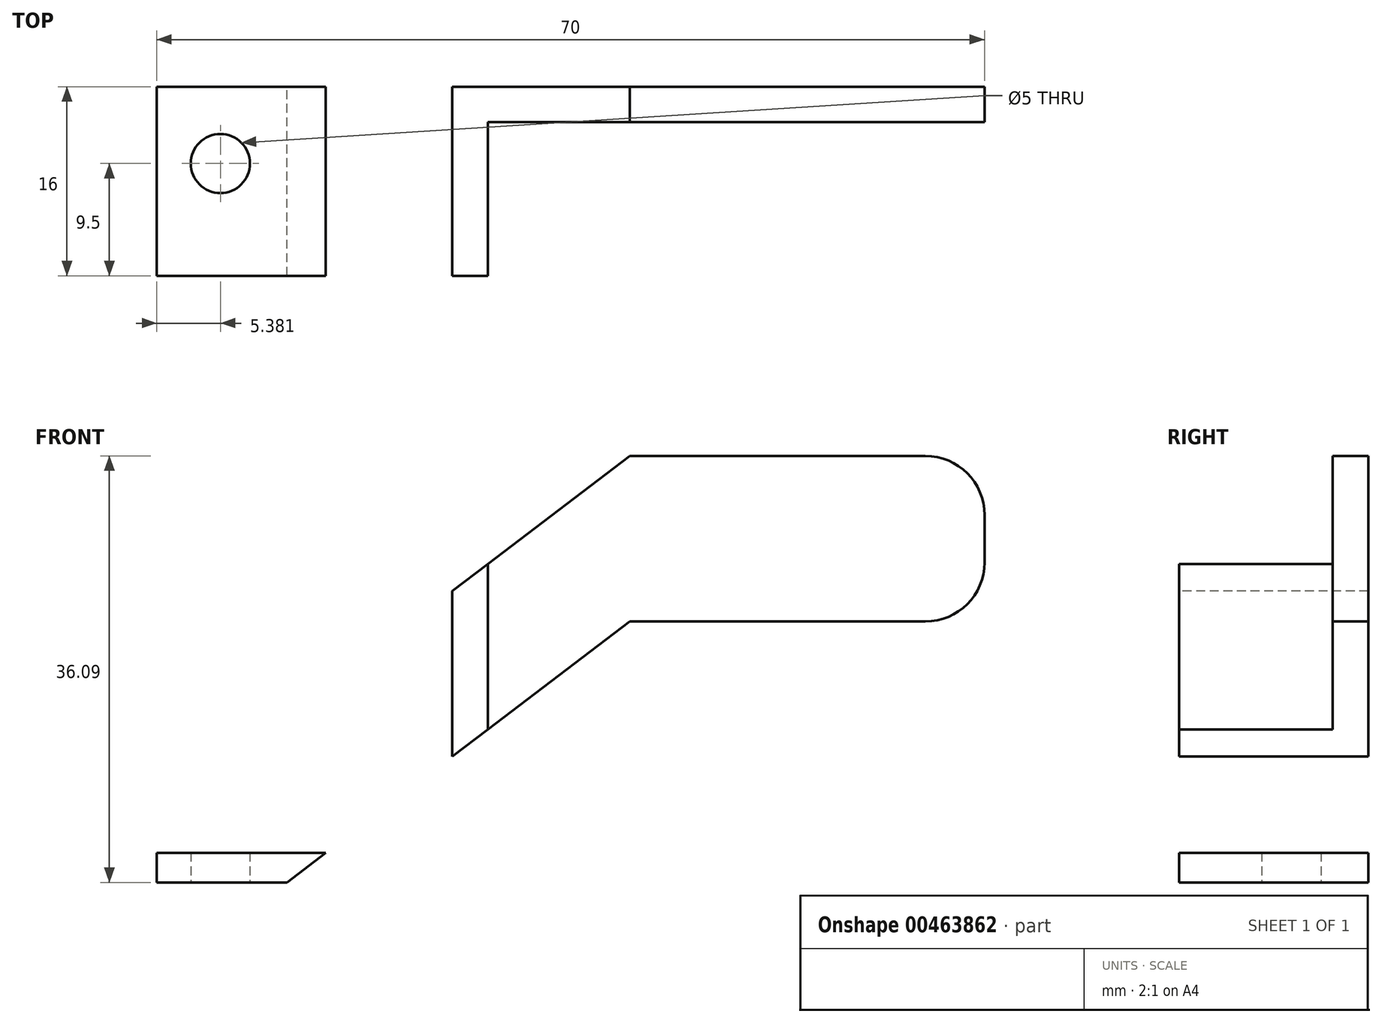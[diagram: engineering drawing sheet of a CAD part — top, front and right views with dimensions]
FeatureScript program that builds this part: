
annotation { "Feature Type Name" : "Feature", "Feature Type Description" : "" }
export const myFeature = defineFeature(function(context is Context, id is Id, definition is map)
    precondition{}
    {
        {
            var Q0;
            Q0=qCreatedBy(makeId("Front.planeOp"),FACE);
            var sketch = newSketch(context, id + "F0", { "sketchPlane" : qUnion([Q0])});
            skLineSegment(sketch, "E0", {"start": v(-8.58, 36.09) * mm, "end": v(16.42, 36.09) * mm});
            skLineSegment(sketch, "E1", {"start": v(21.42, 31.09) * mm, "end": v(21.42, 27.09) * mm});
            skLineSegment(sketch, "E2", {"start": v(16.42, 22.09) * mm, "end": v(-8.58, 22.09) * mm});
            skLineSegment(sketch, "E3", {"start": v(-8.58, 36.09) * mm, "end": v(-8.58, -20.54) * mm, "construction": true});
            skLineSegment(sketch, "E4", {"start": v(-8.58, -20.54) * mm, "end": v(-8.58, 69.46) * mm, "construction": true});
            skLineSegment(sketch, "E5", {"start": v(-8.58, 22.09) * mm, "end": v(-37.58, 0) * mm});
            skLineSegment(sketch, "E6", {"start": v(-37.58, 0) * mm, "end": v(-48.58, 0) * mm});
            skLineSegment(sketch, "E7", {"start": v(-8.58, 36.09) * mm, "end": v(-48.58, 5.62) * mm});
            skLineSegment(sketch, "E8", {"start": v(-48.58, 5.62) * mm, "end": v(-48.58, 0) * mm});
            skPoint(sketch, "E9.visualSharp", {"position": v(21.42, 36.09) * mm});
            skArc(sketch, "E9.filletArc", {"start": v(21.42, 31.09) * mm, "mid": v(19.96, 34.62) * mm, "end": v(16.42, 36.09) * mm});
            skPoint(sketch, "E10.visualSharp", {"position": v(21.42, 22.09) * mm});
            skArc(sketch, "E10.filletArc", {"start": v(16.42, 22.09) * mm, "mid": v(19.96, 23.55) * mm, "end": v(21.42, 27.09) * mm});
            skLineSegment(sketch, "E11", {"start": v(-23.58, 24.66) * mm, "end": v(-23.58, 10.66) * mm});
            skLineSegment(sketch, "E12", {"start": v(-20.58, 26.95) * mm, "end": v(-20.58, 12.95) * mm});
            skLineSegment(sketch, "E13", {"start": v(-48.58, 2.5) * mm, "end": v(-34.3, 2.5) * mm});
            skLineSegment(sketch, "E14", {"start": v(-48.58, 2.5) * mm, "end": v(-48.58, 0) * mm});
            skLineSegment(sketch, "E15", {"start": v(-37.58, 0) * mm, "end": v(-34.3, 2.5) * mm});
            skSolve(sketch);
        }
        {
            var Q0;
            {var subQ3=sQuery(id+"F0.wireOp",EDGE,"E0");Q0=makeQuery(id+"F0.imprint","IMPRINT",FACE,{"disambiguationData":[TD([[makeQuery(id+"F0.imprint","IMPRINT",EDGE,{"derivedFrom":subQ3}),-1.0]])]});}
            var Q1;
            {var subQ0=sQuery(id+"F0.wireOp",EDGE,"E11");Q1=makeQuery(id+"F0.imprint","IMPRINT",FACE,{"disambiguationData":[TD([[makeQuery(id+"F0.imprint","IMPRINT",EDGE,{"derivedFrom":subQ0}),1.0]])]});}
            extrude(context, id + "F1", {"entities" : qUnion([Q0, Q1]), "oppositeDirection" : true, "depth" : 3 * mm});
        }
        {
            var Q0;
            {var subQ0=sQuery(id+"F0.wireOp",EDGE,"E11");Q0=makeQuery(id+"F0.imprint","IMPRINT",FACE,{"disambiguationData":[TD([[makeQuery(id+"F0.imprint","IMPRINT",EDGE,{"derivedFrom":subQ0}),1.0]])]});}
            extrude(context, id + "F2", {"entities" : qUnion([Q0]), "operationType" : NewBodyOperationType.ADD, "depth" : 13 * mm});
        }
        {
            var Q0;
            Q0=makeQuery(id+"F0.imprint","IMPRINT",FACE,{"disambiguationData":[TD([[makeQuery(id+"F0.imprint","IMPRINT",EDGE,{"derivedFrom":sQuery(id+"F0.wireOp",EDGE,"E6")}),-1.0]])]});
            extrude(context, id + "F3", {"entities" : qUnion([Q0]), "depth" : 13 * mm});
        }
        {
            var Q0;
            {var subQ1=sQuery(id+"F0.wireOp",EDGE,"E8");Q0=makeQuery(id+"F0.imprint","IMPRINT",FACE,{"disambiguationData":[TD([[makeQuery(id+"F0.imprint","IMPRINT",EDGE,{"derivedFrom":subQ1}),1.0]])]});}
            extrude(context, id + "F4", {"entities" : qUnion([Q0]), "operationType" : NewBodyOperationType.ADD, "depth" : 13 * mm, "hasSecondDirection" : true, "secondDirectionOppositeDirection" : false, "secondDirectionDepth" : 10 * mm});
        }
        {
            var Q0;
            Q0=makeQuery(id+"F0.imprint","IMPRINT",FACE,{"disambiguationData":[TD([[makeQuery(id+"F0.imprint","IMPRINT",EDGE,{"derivedFrom":sQuery(id+"F0.wireOp",EDGE,"E6")}),-1.0]])]});
            extrude(context, id + "F5", {"entities" : qUnion([Q0]), "operationType" : NewBodyOperationType.ADD, "oppositeDirection" : true, "depth" : 3 * mm});
        }
        {
            var Q0;
            {var subQ0=sQuery(id+"F0.wireOp",EDGE,"E6");Q0=makeQuery(id+"F5.boolean.opBoolean","MERGE",FACE,{"derivedFrom":[makeQuery(id+"F3.opExtrude","SWEPT_FACE",FACE,{"disambiguationData":[OSD([subQ0])]}),makeQuery(id+"F5.opExtrude","SWEPT_FACE",FACE,{"disambiguationData":[OSD([subQ0])]})]});}
            var sketch = newSketch(context, id + "F6", { "sketchPlane" : qUnion([Q0])});
            skCircle(sketch, "E16", {"center": v(-43.2, 3.5) * mm, "radius": 2.5 * mm});
            skSolve(sketch);
        }
        {
            var Q0;
            Q0=makeQuery(id+"F6.imprint","IMPRINT",FACE,{"disambiguationData":[TD([[makeQuery(id+"F6.imprint","IMPRINT",EDGE,{"derivedFrom":sQuery(id+"F6.wireOp",EDGE,"E16")}),1.0]])]});
            extrude(context, id + "F7", {"entities" : qUnion([Q0]), "operationType" : NewBodyOperationType.REMOVE, "oppositeDirection" : true, "depth" : 25 * mm});
        }
    });
